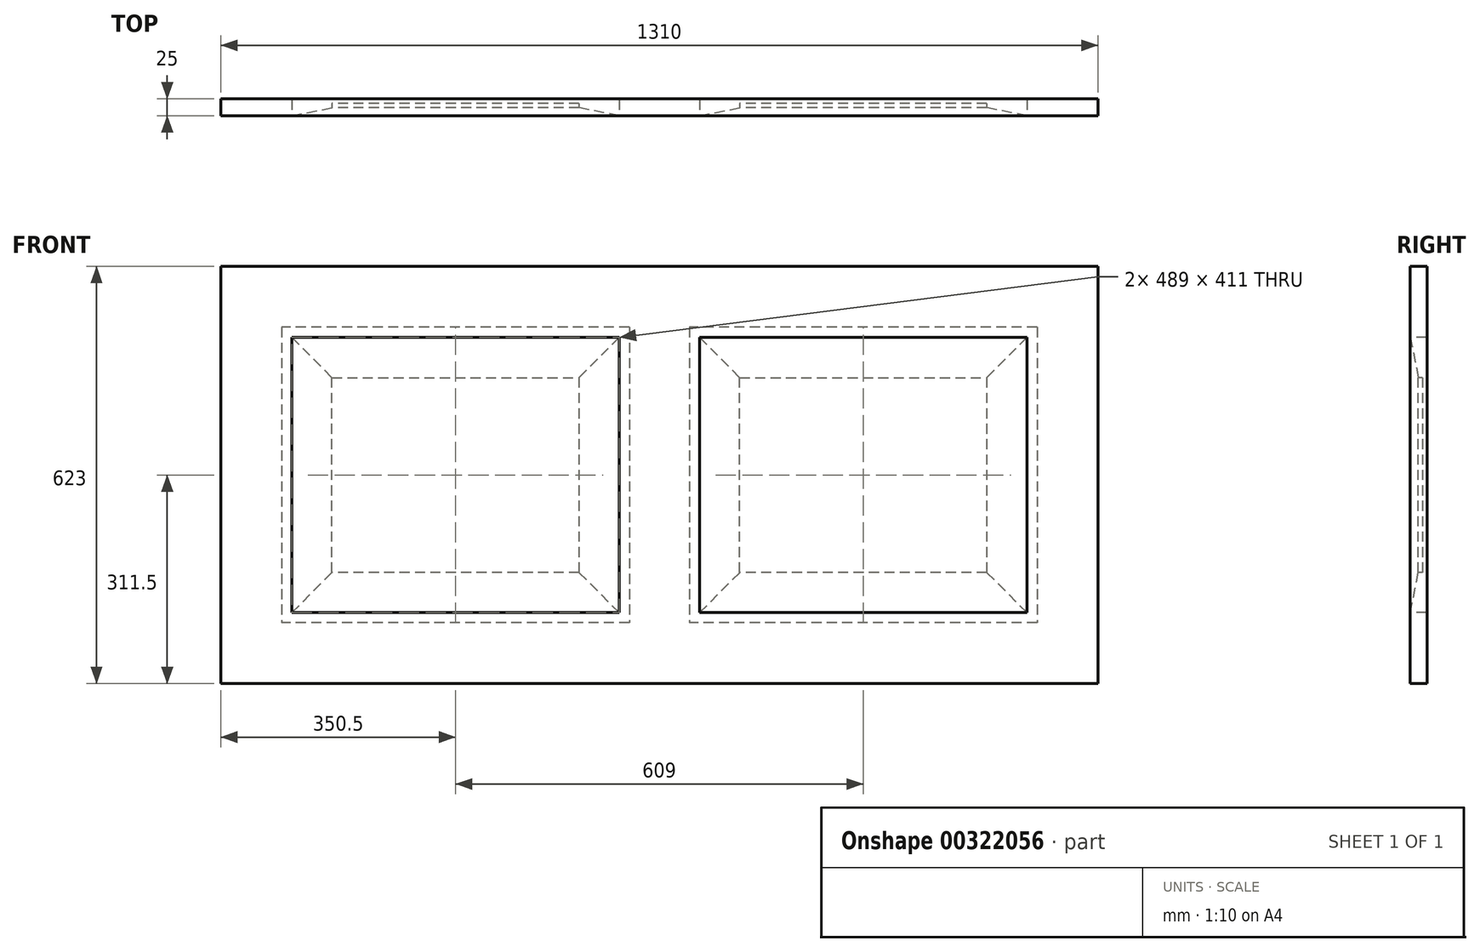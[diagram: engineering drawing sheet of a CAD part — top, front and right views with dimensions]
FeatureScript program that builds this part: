
annotation { "Feature Type Name" : "Feature", "Feature Type Description" : "" }
export const myFeature = defineFeature(function(context is Context, id is Id, definition is map)
    precondition{}
    {
        {
            var Q0;
            Q0=qCreatedBy(makeId("Front.planeOp"),FACE);
            var sketch = newSketch(context, id + "F0", { "sketchPlane" : qUnion([Q0])});
            skLineSegment(sketch, "E0.bottom", {"start": v(655, 0) * mm, "end": v(-655, 0) * mm});
            skLineSegment(sketch, "E0.top", {"start": v(655, -623) * mm, "end": v(-655, -623) * mm});
            skLineSegment(sketch, "E0.left", {"start": v(655, 0) * mm, "end": v(655, -623) * mm});
            skLineSegment(sketch, "E0.right", {"start": v(-655, 0) * mm, "end": v(-655, -623) * mm});
            skLineSegment(sketch, "E1.0", {"start": v(564, -91) * mm, "end": v(45, -91) * mm});
            skLineSegment(sketch, "E1.1", {"start": v(564, -91) * mm, "end": v(564, -532) * mm});
            skLineSegment(sketch, "E1.2", {"start": v(564, -532) * mm, "end": v(45, -532) * mm});
            skLineSegment(sketch, "E1.3", {"start": v(-564, -91) * mm, "end": v(-564, -532) * mm});
            skLineSegment(sketch, "E2", {"start": v(-45, -91) * mm, "end": v(-45, -532) * mm});
            skLineSegment(sketch, "E3", {"start": v(45, -91) * mm, "end": v(45, -532) * mm});
            skLineSegment(sketch, "E4.trimOffspring", {"start": v(-45, -91) * mm, "end": v(-564, -91) * mm});
            skLineSegment(sketch, "E5.trimOffspring", {"start": v(-45, -532) * mm, "end": v(-564, -532) * mm});
            skLineSegment(sketch, "E6.0", {"start": v(549, -106) * mm, "end": v(60, -106) * mm});
            skLineSegment(sketch, "E6.1", {"start": v(549, -106) * mm, "end": v(549, -517) * mm});
            skLineSegment(sketch, "E6.2", {"start": v(549, -517) * mm, "end": v(60, -517) * mm});
            skLineSegment(sketch, "E6.3", {"start": v(60, -106) * mm, "end": v(60, -517) * mm});
            skLineSegment(sketch, "E7.0", {"start": v(-60, -106) * mm, "end": v(-549, -106) * mm});
            skLineSegment(sketch, "E7.1", {"start": v(-60, -106) * mm, "end": v(-60, -517) * mm});
            skLineSegment(sketch, "E7.2", {"start": v(-60, -517) * mm, "end": v(-549, -517) * mm});
            skLineSegment(sketch, "E7.3", {"start": v(-549, -106) * mm, "end": v(-549, -517) * mm});
            skLineSegment(sketch, "E8.0", {"start": v(489, -166) * mm, "end": v(120, -166) * mm});
            skLineSegment(sketch, "E8.1", {"start": v(489, -166) * mm, "end": v(489, -457) * mm});
            skLineSegment(sketch, "E8.2", {"start": v(489, -457) * mm, "end": v(120, -457) * mm});
            skLineSegment(sketch, "E8.3", {"start": v(120, -166) * mm, "end": v(120, -457) * mm});
            skLineSegment(sketch, "E9.0", {"start": v(-120, -166) * mm, "end": v(-489, -166) * mm});
            skLineSegment(sketch, "E9.1", {"start": v(-120, -166) * mm, "end": v(-120, -457) * mm});
            skLineSegment(sketch, "E9.2", {"start": v(-120, -457) * mm, "end": v(-489, -457) * mm});
            skLineSegment(sketch, "E9.3", {"start": v(-489, -166) * mm, "end": v(-489, -457) * mm});
            skLineSegment(sketch, "E10", {"start": v(489, -166) * mm, "end": v(549, -106) * mm});
            skLineSegment(sketch, "E11", {"start": v(120, -166) * mm, "end": v(60, -106) * mm});
            skLineSegment(sketch, "E12", {"start": v(120, -457) * mm, "end": v(60, -517) * mm});
            skLineSegment(sketch, "E13", {"start": v(489, -457) * mm, "end": v(549, -517) * mm});
            skLineSegment(sketch, "E14", {"start": v(-120, -166) * mm, "end": v(-60, -106) * mm});
            skLineSegment(sketch, "E15", {"start": v(-489, -166) * mm, "end": v(-549, -106) * mm});
            skLineSegment(sketch, "E16", {"start": v(-489, -457) * mm, "end": v(-549, -517) * mm});
            skLineSegment(sketch, "E17", {"start": v(-120, -457) * mm, "end": v(-60, -517) * mm});
            skSolve(sketch);
        }
        {
            var Q0;
            Q0=makeQuery(id+"F0.imprint","IMPRINT",FACE,{"disambiguationData":[TD([[makeQuery(id+"F0.imprint","IMPRINT",EDGE,{"derivedFrom":sQuery(id+"F0.wireOp",EDGE,"E0.bottom")}),1.0]])]});
            extrude(context, id + "F1", {"entities" : qUnion([Q0]), "oppositeDirection" : true, "depth" : 25 * mm});
        }
        {
            var Q0;
            Q0=makeQuery(id+"F0.imprint","IMPRINT",FACE,{"disambiguationData":[TD([[makeQuery(id+"F0.imprint","IMPRINT",EDGE,{"derivedFrom":sQuery(id+"F0.wireOp",EDGE,"E1.0")}),1.0]])]});
            var Q1;
            Q1=makeQuery(id+"F0.imprint","IMPRINT",FACE,{"disambiguationData":[TD([[makeQuery(id+"F0.imprint","IMPRINT",EDGE,{"derivedFrom":sQuery(id+"F0.wireOp",EDGE,"E1.3")}),1.0]])]});
            extrude(context, id + "F2", {"entities" : qUnion([Q0, Q1]), "operationType" : NewBodyOperationType.ADD, "oppositeDirection" : true, "depth" : 24 * mm});
        }
        {
            var Q0;
            Q0=makeQuery(id+"F0.imprint","IMPRINT",FACE,{"disambiguationData":[TD([[makeQuery(id+"F0.imprint","IMPRINT",EDGE,{"derivedFrom":sQuery(id+"F0.wireOp",EDGE,"E8.0")}),1.0]])]});
            var Q1;
            Q1=makeQuery(id+"F0.imprint","IMPRINT",FACE,{"disambiguationData":[TD([[makeQuery(id+"F0.imprint","IMPRINT",EDGE,{"derivedFrom":sQuery(id+"F0.wireOp",EDGE,"E9.0")}),1.0]])]});
            extrude(context, id + "F3", {"entities" : qUnion([Q0, Q1]), "operationType" : NewBodyOperationType.REMOVE, "oppositeDirection" : true, "depth" : 22 * mm});
        }
        {
            var Q0;
            Q0=sQuery(id+"F0.wireOp",EDGE,"E8.0");
            cPoint(context, id + "F4", {"entities" : qUnion([Q0]), "parameter" : 0.5});
        }
        {
            var Q0;
            Q0=sQuery(id+"F0.wireOp",EDGE,"E8.2");
            cPoint(context, id + "F5", {"entities" : qUnion([Q0]), "parameter" : 0.5});
        }
        {
            var Q0;
            Q0 = qCreatedBy(id + "F4" ,VERTEX);
            var Q1;
            Q1 = qCreatedBy(id + "F5" ,VERTEX);
            cPlane(context, id + "F6", {"entities" : qUnion([Q0, Q1]), "cplaneType" : CPlaneType.MID_PLANE, "offset" : 25 * mm, "width" : 150 * mm, "height" : 150 * mm});
        }
        {
            var Q0;
            Q0=qCreatedBy(id+"F6.planeOp",FACE);
            var sketch = newSketch(context, id + "F7", { "sketchPlane" : qUnion([Q0])});
            skLineSegment(sketch, "E18", {"start": v(549, 0) * mm, "end": v(60, 0) * mm});
            skLineSegment(sketch, "E19", {"start": v(489, 0) * mm, "end": v(489, -12) * mm});
            skLineSegment(sketch, "E20", {"start": v(489, -12) * mm, "end": v(549, 0) * mm});
            skLineSegment(sketch, "E21", {"start": v(489, -12) * mm, "end": v(489, -15) * mm});
            skSolve(sketch);
        }
        {
            var Q0;
            {var subQ2=sQuery(id+"F7.wireOp",EDGE,"E19");Q0=makeQuery(id+"F7.imprint","IMPRINT",FACE,{"disambiguationData":[TD([[makeQuery(id+"F7.imprint","IMPRINT",EDGE,{"derivedFrom":subQ2}),1.0]])]});}
            var Q1;
            Q1=sQuery(id+"F0.wireOp",EDGE,"E8.1");
            var Q2;
            Q2=sQuery(id+"F0.wireOp",EDGE,"E8.2");
            var Q3;
            Q3=sQuery(id+"F0.wireOp",EDGE,"E8.3");
            var Q4;
            Q4=sQuery(id+"F0.wireOp",EDGE,"E8.0");
            sweep(context, id + "F8", {"profiles" : qUnion([Q0]), "path" : qUnion([Q1, Q2, Q3, Q4])});
        }
        {
            var Q0;
            Q0=makeQuery(id+"F0.imprint","IMPRINT",FACE,{"disambiguationData":[TD([[makeQuery(id+"F0.imprint","IMPRINT",EDGE,{"derivedFrom":sQuery(id+"F0.wireOp",EDGE,"E8.0")}),1.0]])]});
            extrude(context, id + "F9", {"entities" : qUnion([Q0]), "operationType" : NewBodyOperationType.ADD, "oppositeDirection" : true, "depth" : 18 * mm});
        }
        {
            var Q0;
            Q0=makeQuery(id+"F8.opSweep","SWEPT_BODY",BODY,{"disambiguationData":[OSD([sQuery(id+"F0.wireOp",EDGE,"E8.0"),sQuery(id+"F7.wireOp",EDGE,"E18"),sQuery(id+"F7.wireOp",EDGE,"E19"),sQuery(id+"F7.wireOp",EDGE,"E20")])]});
            var Q1;
            Q1=sQuery(id+"F0.wireOp",VERTEX,"E1.1.start");
            var Q2;
            Q2=sQuery(id+"F0.wireOp",VERTEX,"E2.start");
            transform(context, id + "F10", {"entities" : qUnion([Q0]), "transformType" : TransformType.TRANSLATION_ENTITY, "oppositeDirectionEntity" : false, "transformLine" : qUnion([Q1, Q2]), "makeCopy" : true});
        }
    });
